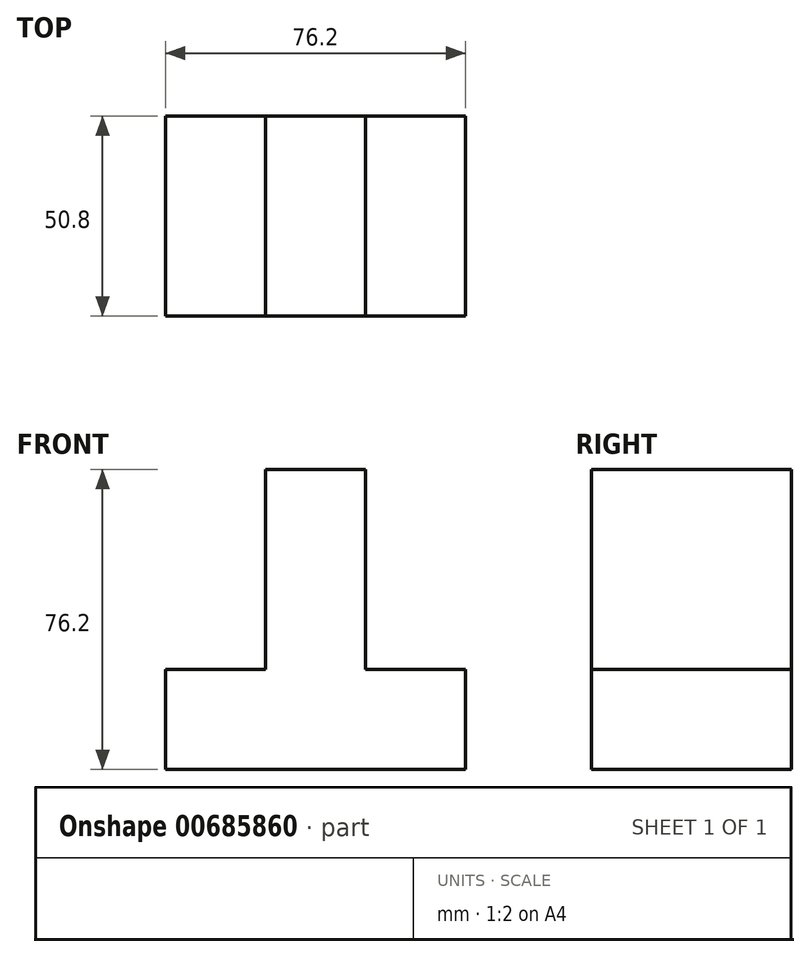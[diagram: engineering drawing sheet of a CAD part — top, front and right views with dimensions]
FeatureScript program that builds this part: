
annotation { "Feature Type Name" : "Feature", "Feature Type Description" : "" }
export const myFeature = defineFeature(function(context is Context, id is Id, definition is map)
    precondition{}
    {
        {
            var Q0;
            Q0=qCreatedBy(makeId("Front.planeOp"),FACE);
            var sketch = newSketch(context, id + "F0", { "sketchPlane" : qUnion([Q0])});
            skLineSegment(sketch, "E0", {"start": v(-36, -21.86) * mm, "end": v(40.2, -21.86) * mm});
            skLineSegment(sketch, "E1", {"start": v(-36, -21.86) * mm, "end": v(-36, 3.54) * mm});
            skLineSegment(sketch, "E2", {"start": v(-36, 3.54) * mm, "end": v(-10.6, 3.54) * mm});
            skLineSegment(sketch, "E3", {"start": v(-10.6, 3.54) * mm, "end": v(-10.6, 54.34) * mm});
            skLineSegment(sketch, "E4", {"start": v(-10.6, 54.34) * mm, "end": v(14.8, 54.34) * mm});
            skLineSegment(sketch, "E5", {"start": v(14.8, 54.34) * mm, "end": v(14.8, 3.54) * mm});
            skLineSegment(sketch, "E6", {"start": v(14.8, 3.54) * mm, "end": v(40.2, 3.54) * mm});
            skLineSegment(sketch, "E7", {"start": v(40.2, 3.54) * mm, "end": v(40.2, -21.86) * mm});
            skSolve(sketch);
        }
        {
            var Q0;
            Q0 = qSketchRegion(id + "F0", true);
            extrude(context, id + "F1", {"entities" : qUnion([Q0]), "depth" : 50.8 * mm, "offsetDistance" : 25.4 * mm});
        }
    });
